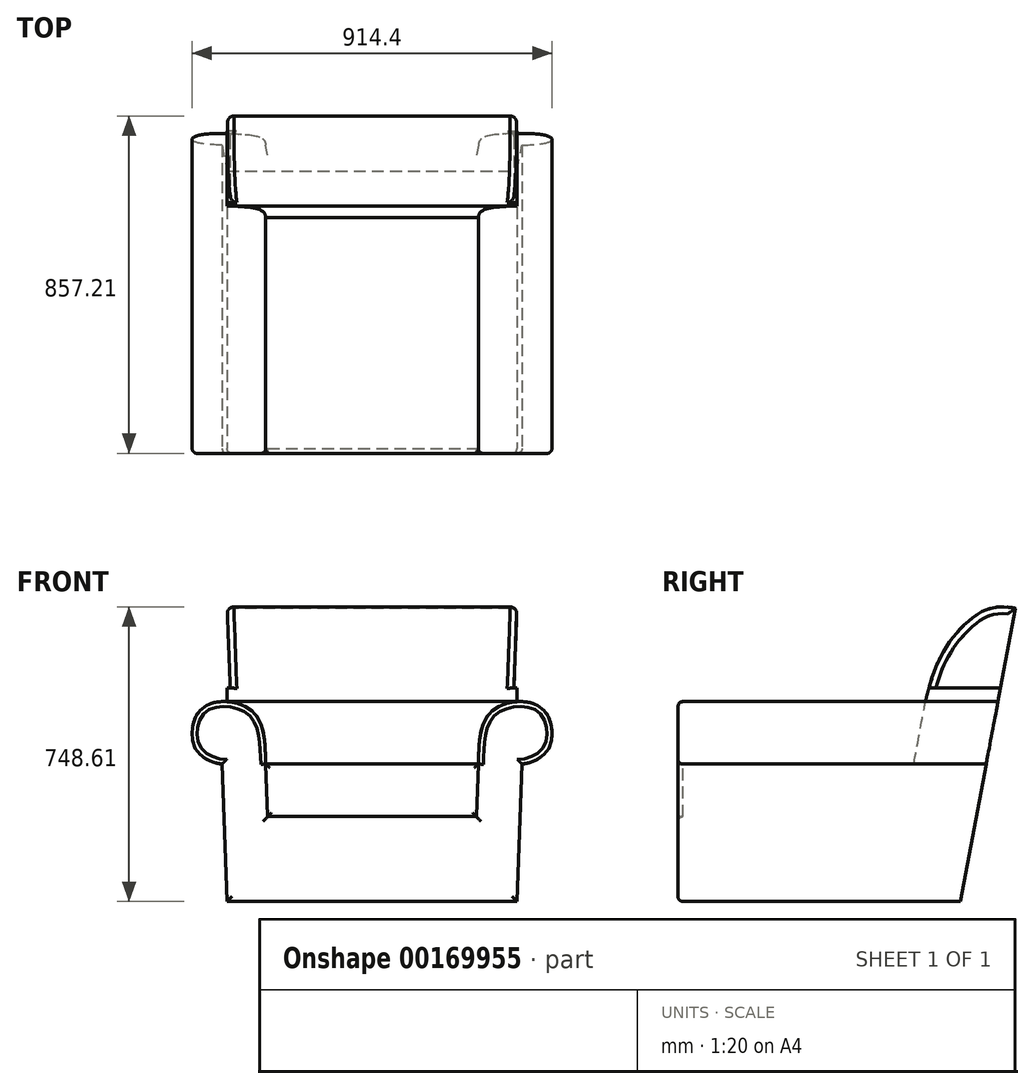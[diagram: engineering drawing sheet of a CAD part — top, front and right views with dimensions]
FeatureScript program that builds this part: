
annotation { "Feature Type Name" : "Feature", "Feature Type Description" : "" }
export const myFeature = defineFeature(function(context is Context, id is Id, definition is map)
    precondition{}
    {
        {
            var Q0;
            Q0=qCreatedBy(makeId("Front.planeOp"),FACE);
            var sketch = newSketch(context, id + "F0", { "sketchPlane" : qUnion([Q0])});
            skLineSegment(sketch, "E0", {"start": v(-368.3, -163.65) * mm, "end": v(368.3, -163.65) * mm});
            skLineSegment(sketch, "E1", {"start": v(-368.3, -163.65) * mm, "end": v(-381, 185.6) * mm});
            skLineSegment(sketch, "E2", {"start": v(381, 185.6) * mm, "end": v(368.3, -163.65) * mm});
            skLineSegment(sketch, "E3", {"start": v(-269.88, 185.6) * mm, "end": v(-265.03, 52.25) * mm});
            skLineSegment(sketch, "E4", {"start": v(-265.03, 52.25) * mm, "end": v(265.03, 52.25) * mm});
            skLineSegment(sketch, "E5", {"start": v(265.03, 52.25) * mm, "end": v(269.88, 185.6) * mm});
            skPoint(sketch, "E6", {"position": v(0, 52.25) * mm});
            skPoint(sketch, "E7", {"position": v(0, -163.65) * mm});
            skFitSpline(sketch, "E8", {"points": [v(269.88, 185.6) * mm, v(301.71, 317.05) * mm, v(428.37, 329.82) * mm, v(454.24, 239.6) * mm, v(420.79, 198.22) * mm, v(381, 185.6) * mm], "startDerivative": vector(24.12, 514.5) * mm, "endDerivative": vector(-224.77, -9.04) * mm});
            skLineSegment(sketch, "E9", {"start": v(234, 344.35) * mm, "end": v(456.81, 344.35) * mm, "construction": true});
            skLineSegment(sketch, "E10", {"start": v(457.2, 357.55) * mm, "end": v(457.2, 234.11) * mm, "construction": true});
            skLineSegment(sketch, "E11", {"start": v(0, 321) * mm, "end": v(0, 157.04) * mm, "construction": true});
            skFitSpline(sketch, "E12.MirrorCS", {"points": [v(-269.88, 185.6) * mm, v(-301.71, 317.05) * mm, v(-428.37, 329.82) * mm, v(-454.24, 239.6) * mm, v(-420.79, 198.22) * mm, v(-381, 185.6) * mm], "startDerivative": vector(-24.12, 514.5) * mm, "endDerivative": vector(224.77, -9.04) * mm});
            skSolve(sketch);
        }
        {
            var Q0;
            Q0=makeQuery(id+"F0.imprint","IMPRINT",FACE,{"disambiguationData":[TD([[makeQuery(id+"F0.imprint","IMPRINT",EDGE,{"derivedFrom":sQuery(id+"F0.wireOp",EDGE,"E0")}),1.0]])]});
            extrude(context, id + "F1", {"entities" : qUnion([Q0]), "oppositeDirection" : true, "depth" : 812.8 * mm});
        }
        {
            var Q0;
            Q0=qCreatedBy(makeId("Right.planeOp"),FACE);
            var sketch = newSketch(context, id + "F2", { "sketchPlane" : qUnion([Q0])});
            skLineSegment(sketch, "E13", {"start": v(812.8, 343.38) * mm, "end": v(717.55, -163.65) * mm});
            skLineSegment(sketch, "E14", {"start": v(717.55, -163.65) * mm, "end": v(717.55, -180.75) * mm});
            skLineSegment(sketch, "E15", {"start": v(717.55, -180.75) * mm, "end": v(830.02, -180.75) * mm});
            skLineSegment(sketch, "E16", {"start": v(830.02, -180.75) * mm, "end": v(830.02, 343.38) * mm});
            skLineSegment(sketch, "E17", {"start": v(830.02, 343.38) * mm, "end": v(812.8, 343.38) * mm});
            skSolve(sketch);
        }
        {
            var Q0;
            Q0=makeQuery(id+"F2.imprint","IMPRINT",FACE,{"disambiguationData":[TD([[makeQuery(id+"F2.imprint","IMPRINT",EDGE,{"derivedFrom":sQuery(id+"F2.wireOp",EDGE,"E13")}),1.0]])]});
            extrude(context, id + "F3", {"entities" : qUnion([Q0]), "operationType" : NewBodyOperationType.REMOVE, "endBound" : BoundingType.SYMMETRIC, "oppositeDirection" : true, "depth" : 1219.2 * mm});
        }
        {
            var Q0;
            Q0=qCreatedBy(makeId("Right.planeOp"),FACE);
            var sketch = newSketch(context, id + "F4", { "sketchPlane" : qUnion([Q0])});
            skPoint(sketch, "E18.0", {"position": v(758.1, 52.25) * mm});
            skLineSegment(sketch, "E19", {"start": v(758.1, 52.25) * mm, "end": v(857.2, 581.53) * mm});
            skLineSegment(sketch, "E20", {"start": v(0, 344.35) * mm, "end": v(812.8, 344.35) * mm, "construction": true});
            skLineSegment(sketch, "E21.0", {"start": v(758.1, 52.25) * mm, "end": v(0, 52.25) * mm, "construction": true});
            skLineSegment(sketch, "E22", {"start": v(84.79, 179.25) * mm, "end": v(861.12, 179.25) * mm, "construction": true});
            skFitSpline(sketch, "E23", {"points": [v(857.2, 581.53) * mm, v(767.16, 569.77) * mm, v(687.44, 491.95) * mm, v(628.65, 344.35) * mm], "startDerivative": vector(-409.99, 73.48) * mm, "endDerivative": vector(-132.5, -535.48) * mm});
            skLineSegment(sketch, "E24", {"start": v(628.65, 344.35) * mm, "end": v(573.96, 52.25) * mm});
            skLineSegment(sketch, "E25", {"start": v(573.96, 52.25) * mm, "end": v(758.1, 52.25) * mm});
            skSolve(sketch);
        }
        {
            var Q0;
            Q0=makeQuery(id+"F4.imprint","IMPRINT",FACE,{"disambiguationData":[TD([[makeQuery(id+"F4.imprint","IMPRINT",EDGE,{"derivedFrom":sQuery(id+"F4.wireOp",EDGE,"E19")}),1.0]])]});
            extrude(context, id + "F5", {"entities" : qUnion([Q0]), "operationType" : NewBodyOperationType.ADD, "endBound" : BoundingType.SYMMETRIC, "depth" : 736.6 * mm});
        }
        {
            var Q0;
            Q0=makeQuery(id+"F0.imprint","IMPRINT",FACE,{"disambiguationData":[TD([[makeQuery(id+"F0.imprint","IMPRINT",EDGE,{"derivedFrom":sQuery(id+"F0.wireOp",EDGE,"E0")}),1.0]])]});
            var sketch = newSketch(context, id + "F6", { "sketchPlane" : qUnion([Q0])});
            skFitSpline(sketch, "E26.0", {"points": [v(269.88, 185.6) * mm, v(271.9, 228.63) * mm, v(267.64, 341.13) * mm, v(450.12, 358.81) * mm, v(465.5, 235.12) * mm, v(424.97, 195.93) * mm, v(391.44, 186.02) * mm, v(381, 185.6) * mm]});
            skLineSegment(sketch, "E27", {"start": v(-368.3, 584.96) * mm, "end": v(368.3, 584.96) * mm, "construction": true});
            skLineSegment(sketch, "E28", {"start": v(368.3, 584.96) * mm, "end": v(368.3, 344.06) * mm});
            skLineSegment(sketch, "E29", {"start": v(368.3, 584.96) * mm, "end": v(358.78, 343.03) * mm});
            skLineSegment(sketch, "E30.0", {"start": v(0, 321) * mm, "end": v(0, 157.04) * mm, "construction": true});
            skLineSegment(sketch, "E31.MirrorCS", {"start": v(-368.3, 584.96) * mm, "end": v(-358.78, 343.03) * mm});
            skLineSegment(sketch, "E32.MirrorCS", {"start": v(-368.3, 584.96) * mm, "end": v(-368.3, 344.06) * mm});
            skFitSpline(sketch, "E33.MirrorCS", {"points": [v(-269.88, 185.6) * mm, v(-271.9, 228.63) * mm, v(-267.64, 341.13) * mm, v(-450.12, 358.81) * mm, v(-465.5, 235.12) * mm, v(-424.97, 195.93) * mm, v(-391.44, 186.02) * mm, v(-381, 185.6) * mm]});
            skSolve(sketch);
        }
        {
            var Q0;
            {var subQ0=sQuery(id+"F6.wireOp",EDGE,"E31.MirrorCS");Q0=makeQuery(id+"F6.imprint","IMPRINT",FACE,{"disambiguationData":[TD([[makeQuery(id+"F6.imprint","IMPRINT",EDGE,{"derivedFrom":subQ0}),-1.0]])]});}
            var Q1;
            {var subQ0=sQuery(id+"F6.wireOp",EDGE,"E28");Q1=makeQuery(id+"F6.imprint","IMPRINT",FACE,{"disambiguationData":[TD([[makeQuery(id+"F6.imprint","IMPRINT",EDGE,{"derivedFrom":subQ0}),-1.0]])]});}
            extrude(context, id + "F7", {"entities" : qUnion([Q0, Q1]), "operationType" : NewBodyOperationType.REMOVE, "endBound" : BoundingType.THROUGH_ALL, "oppositeDirection" : true, "depth" : 25.4 * mm});
        }
        {
            var Q0;
            Q0=makeQuery(id+"F1.opExtrude","CAP_FACE",FACE,{"disambiguationData":[OSD([sQuery(id+"F0.wireOp",EDGE,"E0"),sQuery(id+"F0.wireOp",EDGE,"E1"),sQuery(id+"F0.wireOp",EDGE,"E2"),sQuery(id+"F0.wireOp",EDGE,"E3"),sQuery(id+"F0.wireOp",EDGE,"E4"),sQuery(id+"F0.wireOp",EDGE,"E5"),sQuery(id+"F0.wireOp",EDGE,"E8"),sQuery(id+"F0.wireOp",EDGE,"E12.MirrorCS")])],"isStart":true});
            fillet(context, id + "F8", {"entities" : qUnion([Q0]), "radius" : 12.7 * mm, "tangentPropagation" : true, "allowEdgeOverflow" : false});
        }
        {
            var Q0;
            Q0=makeQuery(id+"F0.imprint","IMPRINT",FACE,{"disambiguationData":[TD([[makeQuery(id+"F0.imprint","IMPRINT",EDGE,{"derivedFrom":sQuery(id+"F0.wireOp",EDGE,"E0")}),1.0]])]});
            var sketch = newSketch(context, id + "F9", { "sketchPlane" : qUnion([Q0])});
            skLineSegment(sketch, "E34.0", {"start": v(-269.88, 185.6) * mm, "end": v(-265.03, 52.25) * mm});
            skLineSegment(sketch, "E35.0", {"start": v(-265.03, 52.25) * mm, "end": v(265.03, 52.25) * mm});
            skLineSegment(sketch, "E36.0", {"start": v(265.03, 52.25) * mm, "end": v(269.88, 185.6) * mm});
            skLineSegment(sketch, "E37", {"start": v(-269.88, 185.6) * mm, "end": v(269.88, 185.6) * mm});
            skSolve(sketch);
        }
        {
            var Q0;
            Q0=makeQuery(id+"F9.imprint","IMPRINT",FACE,{"disambiguationData":[TD([[makeQuery(id+"F9.imprint","IMPRINT",EDGE,{"derivedFrom":sQuery(id+"F9.wireOp",EDGE,"E34.0")}),1.0]])]});
            extrude(context, id + "F10", {"entities" : qUnion([Q0]), "operationType" : NewBodyOperationType.ADD, "oppositeDirection" : true, "depth" : 673.1 * mm});
        }
        {
            var Q0;
            Q0=makeQuery(id+"F10.opExtrude","CAP_FACE",FACE,{"disambiguationData":[OSD([sQuery(id+"F9.wireOp",EDGE,"E34.0"),sQuery(id+"F9.wireOp",EDGE,"E35.0"),sQuery(id+"F9.wireOp",EDGE,"E36.0"),sQuery(id+"F9.wireOp",EDGE,"E37")])],"isStart":true});
            fillet(context, id + "F11", {"entities" : qUnion([Q0]), "radius" : 8.9 * mm, "tangentPropagation" : true, "allowEdgeOverflow" : false});
        }
        {
            var Q0;
            Q0=makeQuery(id+"F7.boolean.opBoolean","INTERSECT",EDGE,{"derivedFrom":[makeQuery(id+"F5.opExtrude","SWEPT_FACE",FACE,{"disambiguationData":[OSD([sQuery(id+"F4.wireOp",EDGE,"E23")])]}),makeQuery(id+"F7.opExtrude","SWEPT_FACE",FACE,{"disambiguationData":[OSD([sQuery(id+"F6.wireOp",EDGE,"E29")])]})]});
            var Q1;
            Q1=makeQuery(id+"F7.boolean.opBoolean","INTERSECT",EDGE,{"derivedFrom":[makeQuery(id+"F5.opExtrude","SWEPT_FACE",FACE,{"disambiguationData":[OSD([sQuery(id+"F4.wireOp",EDGE,"E19")])]}),makeQuery(id+"F7.opExtrude","SWEPT_FACE",FACE,{"disambiguationData":[OSD([sQuery(id+"F6.wireOp",EDGE,"E29")])]})]});
            var Q2;
            Q2=makeQuery(id+"F7.boolean.opBoolean","INTERSECT",EDGE,{"derivedFrom":[makeQuery(id+"F5.opExtrude","SWEPT_FACE",FACE,{"disambiguationData":[OSD([sQuery(id+"F4.wireOp",EDGE,"E19")])]}),makeQuery(id+"F7.opExtrude","SWEPT_FACE",FACE,{"disambiguationData":[OSD([sQuery(id+"F6.wireOp",EDGE,"E31.MirrorCS")])]})]});
            var Q3;
            Q3=makeQuery(id+"F7.boolean.opBoolean","INTERSECT",EDGE,{"derivedFrom":[makeQuery(id+"F5.opExtrude","SWEPT_FACE",FACE,{"disambiguationData":[OSD([sQuery(id+"F4.wireOp",EDGE,"E23")])]}),makeQuery(id+"F7.opExtrude","SWEPT_FACE",FACE,{"disambiguationData":[OSD([sQuery(id+"F6.wireOp",EDGE,"E31.MirrorCS")])]})]});
            fillet(context, id + "F12", {"entities" : qUnion([Q0, Q1, Q2, Q3]), "radius" : 16.5 * mm, "tangentPropagation" : true, "allowEdgeOverflow" : false});
        }
    });
